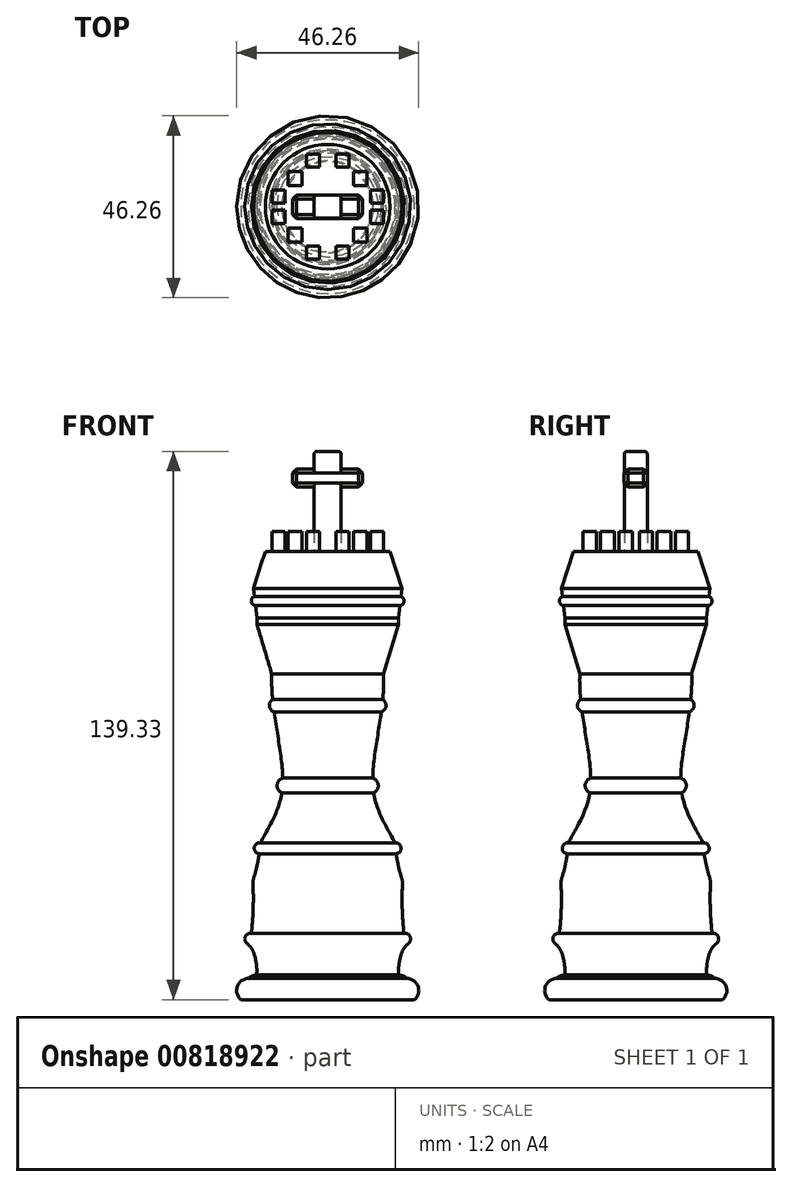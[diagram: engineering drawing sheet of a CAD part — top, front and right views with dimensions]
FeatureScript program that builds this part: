
annotation { "Feature Type Name" : "Feature", "Feature Type Description" : "" }
export const myFeature = defineFeature(function(context is Context, id is Id, definition is map)
    precondition{}
    {
        {
            var Q0;
            Q0=qCreatedBy(makeId("Front.planeOp"),FACE);
            var sketch = newSketch(context, id + "F0", { "sketchPlane" : qUnion([Q0])});
            skLineSegment(sketch, "E0", {"start": v(0, -37.92) * mm, "end": v(0, 63.8) * mm});
            skArc(sketch, "E1", {"start": v(-11.45, 12.13) * mm, "mid": v(-12.85, 10.36) * mm, "end": v(-11.68, 8.42) * mm});
            skArc(sketch, "E2", {"start": v(-14, 32.07) * mm, "mid": v(-14.81, 30.39) * mm, "end": v(-13.62, 28.94) * mm});
            skArc(sketch, "E3", {"start": v(-19.74, -30.2) * mm, "mid": v(-18.98, -22.08) * mm, "end": v(-19.03, -13.92) * mm});
            skFitSpline(sketch, "E4.trimOffspring", {"points": [v(-25.61, -37.92) * mm, v(-19.46, -8.96) * mm, v(-11.68, 8.42) * mm, v(-14.2, 35.39) * mm, v(-12.94, 57.3) * mm, v(-15.84, 63.8) * mm], "startDerivative": vector(16.77, 129.7) * mm, "endDerivative": vector(-31.89, 45.75) * mm});
            skArc(sketch, "E5", {"start": v(-19.03, -13.92) * mm, "mid": v(-17.75, -9.2) * mm, "end": v(-17.15, -4.34) * mm});
            skArc(sketch, "E6", {"start": v(-18.05, -37.92) * mm, "mid": v(-18.31, -33.93) * mm, "end": v(-19.74, -30.2) * mm});
            skArc(sketch, "E7", {"start": v(-17.15, -4.34) * mm, "mid": v(-18.67, -5.58) * mm, "end": v(-17.4, -7.09) * mm});
            skArc(sketch, "E8", {"start": v(-19.38, -27.31) * mm, "mid": v(-21.06, -28.56) * mm, "end": v(-19.74, -30.2) * mm});
            skArc(sketch, "E9", {"start": v(-18.05, -37.92) * mm, "mid": v(-21.18, -41.05) * mm, "end": v(-18.05, -44.17) * mm});
            skArc(sketch, "E10", {"start": v(-20.2, -38.78) * mm, "mid": v(-22.96, -40.84) * mm, "end": v(-22.07, -44.17) * mm});
            skLineSegment(sketch, "E11", {"start": v(-18.05, -44.17) * mm, "end": v(0, -44.17) * mm});
            skLineSegment(sketch, "E12", {"start": v(0, -44.17) * mm, "end": v(0, -37.92) * mm});
            skLineSegment(sketch, "E13", {"start": v(-18.05, -44.17) * mm, "end": v(-22.07, -44.17) * mm});
            skLineSegment(sketch, "E14", {"start": v(-14.2, 38.6) * mm, "end": v(-17.98, 51.2) * mm});
            skLineSegment(sketch, "E15", {"start": v(-15.84, 69.76) * mm, "end": v(0, 69.76) * mm});
            skLineSegment(sketch, "E16", {"start": v(0, 69.76) * mm, "end": v(0, 63.8) * mm});
            skFitSpline(sketch, "E17.trimOffspring", {"points": [v(-25.61, -37.92) * mm, v(-19.46, -8.96) * mm, v(-11.68, 8.42) * mm, v(-14.2, 35.39) * mm, v(-12.94, 57.3) * mm, v(-15.84, 63.8) * mm], "startDerivative": vector(16.77, 129.7) * mm, "endDerivative": vector(-31.89, 45.75) * mm});
            skPoint(sketch, "E18.orphan", {"position": v(-21.75, 63.8) * mm});
            skLineSegment(sketch, "E19", {"start": v(-17.94, 52.8) * mm, "end": v(-18.85, 60.36) * mm});
            skLineSegment(sketch, "E20", {"start": v(-18.85, 60.36) * mm, "end": v(-15.84, 69.76) * mm});
            skLineSegment(sketch, "E21", {"start": v(-17.94, 52.8) * mm, "end": v(-17.98, 51.2) * mm});
            skPoint(sketch, "E22.start.orphan", {"position": v(-18.85, 54.11) * mm});
            skArc(sketch, "E23", {"start": v(-18.6, 58.27) * mm, "mid": v(-19.4, 57) * mm, "end": v(-18.32, 55.95) * mm});
            skSolve(sketch);
        }
        {
            var Q0;
            Q0 = qSketchRegion(id + "F0", true);
            var Q1;
            Q1=sQuery(id+"F0.wireOp",EDGE,"E0");
            revolve(context, id + "F1", {"surfaceOperationType" : NewSurfaceOperationType.NEW, "entities" : qUnion([Q0]), "axis" : qUnion([Q1]), "revolveType" : RevolveType.FULL});
        }
        {
            var Q0;
            Q0=makeQuery(id+"F1.opRevolve","SWEPT_EDGE",EDGE,{"disambiguationData":[OSD([sQuery(id+"F0.wireOp",EDGE,"E3"),sQuery(id+"F0.wireOp",EDGE,"E6")])]});
            var Q1;
            Q1=makeQuery(id+"F1.opRevolve","SWEPT_EDGE",EDGE,{"disambiguationData":[OSD([sQuery(id+"F0.wireOp",EDGE,"E3"),sQuery(id+"F0.wireOp",EDGE,"E5")])]});
            fillet(context, id + "F2", {"entities" : qUnion([Q0, Q1]), "radius" : 5.08 * mm, "tangentPropagation" : true, "allowEdgeOverflow" : false});
        }
        {
            var Q0;
            Q0=makeQuery(id+"F1.opRevolve","SWEPT_FACE",FACE,{"disambiguationData":[OSD([sQuery(id+"F0.wireOp",EDGE,"E15")])]});
            var sketch = newSketch(context, id + "F3", { "sketchPlane" : qUnion([Q0])});
            skLineSegment(sketch, "E24", {"start": v(0, 30.88) * mm, "end": v(0, -30.54) * mm});
            skLineSegment(sketch, "E25", {"start": v(-43.93, 0) * mm, "end": v(35.6, 0) * mm});
            skLineSegment(sketch, "E26.bottom", {"start": v(-5.44, 13.36) * mm, "end": v(-2.12, 13.36) * mm});
            skLineSegment(sketch, "E26.top", {"start": v(-5.44, 10.04) * mm, "end": v(-2.12, 10.04) * mm});
            skLineSegment(sketch, "E26.left", {"start": v(-5.44, 13.36) * mm, "end": v(-5.44, 10.04) * mm});
            skLineSegment(sketch, "E26.right", {"start": v(-2.12, 13.36) * mm, "end": v(-2.12, 10.04) * mm});
            skLineSegment(sketch, "E27.MirrorCS", {"start": v(5.44, 10.04) * mm, "end": v(2.12, 10.04) * mm});
            skLineSegment(sketch, "E28.MirrorCS", {"start": v(5.44, 13.36) * mm, "end": v(5.44, 10.04) * mm});
            skLineSegment(sketch, "E29.MirrorCS", {"start": v(5.44, 13.36) * mm, "end": v(2.12, 13.36) * mm});
            skLineSegment(sketch, "E30.MirrorCS", {"start": v(2.12, 13.36) * mm, "end": v(2.12, 10.04) * mm});
            skLineSegment(sketch, "E31.MirrorCS", {"start": v(-5.44, -10.04) * mm, "end": v(-2.12, -10.04) * mm});
            skLineSegment(sketch, "E32.MirrorCS", {"start": v(-5.44, -13.36) * mm, "end": v(-5.44, -10.04) * mm});
            skLineSegment(sketch, "E33.MirrorCS", {"start": v(-2.12, -13.36) * mm, "end": v(-2.12, -10.04) * mm});
            skLineSegment(sketch, "E34.MirrorCS", {"start": v(-5.44, -13.36) * mm, "end": v(-2.12, -13.36) * mm});
            skLineSegment(sketch, "E35.MirrorCS", {"start": v(2.12, -13.36) * mm, "end": v(2.12, -10.04) * mm});
            skLineSegment(sketch, "E36.MirrorCS", {"start": v(5.44, -13.36) * mm, "end": v(2.12, -13.36) * mm});
            skLineSegment(sketch, "E37.MirrorCS", {"start": v(5.44, -10.04) * mm, "end": v(2.12, -10.04) * mm});
            skLineSegment(sketch, "E38.MirrorCS", {"start": v(5.44, -13.36) * mm, "end": v(5.44, -10.04) * mm});
            skLineSegment(sketch, "E39.bottom", {"start": v(-6.52, 8.95) * mm, "end": v(-10.04, 8.95) * mm});
            skLineSegment(sketch, "E39.top", {"start": v(-6.52, 5.36) * mm, "end": v(-10.04, 5.36) * mm});
            skLineSegment(sketch, "E39.left", {"start": v(-6.52, 8.95) * mm, "end": v(-6.52, 5.36) * mm});
            skLineSegment(sketch, "E39.right", {"start": v(-10.04, 8.95) * mm, "end": v(-10.04, 5.36) * mm});
            skLineSegment(sketch, "E40.MirrorCS", {"start": v(-6.52, -5.36) * mm, "end": v(-10.04, -5.36) * mm});
            skLineSegment(sketch, "E41.MirrorCS", {"start": v(-10.04, -8.95) * mm, "end": v(-10.04, -5.36) * mm});
            skLineSegment(sketch, "E42.MirrorCS", {"start": v(-6.52, -8.95) * mm, "end": v(-6.52, -5.36) * mm});
            skLineSegment(sketch, "E43.MirrorCS", {"start": v(-6.52, -8.95) * mm, "end": v(-10.04, -8.95) * mm});
            skLineSegment(sketch, "E44.MirrorCS", {"start": v(6.52, 8.95) * mm, "end": v(6.52, 5.36) * mm});
            skLineSegment(sketch, "E45.MirrorCS", {"start": v(6.52, 8.95) * mm, "end": v(10.04, 8.95) * mm});
            skLineSegment(sketch, "E46.MirrorCS", {"start": v(10.04, 8.95) * mm, "end": v(10.04, 5.36) * mm});
            skLineSegment(sketch, "E47.MirrorCS", {"start": v(6.52, 5.36) * mm, "end": v(10.04, 5.36) * mm});
            skLineSegment(sketch, "E48.MirrorCS", {"start": v(6.52, -5.36) * mm, "end": v(10.04, -5.36) * mm});
            skLineSegment(sketch, "E49.MirrorCS", {"start": v(10.04, -8.95) * mm, "end": v(10.04, -5.36) * mm});
            skLineSegment(sketch, "E50.MirrorCS", {"start": v(6.52, -8.95) * mm, "end": v(10.04, -8.95) * mm});
            skLineSegment(sketch, "E51.MirrorCS", {"start": v(6.52, -8.95) * mm, "end": v(6.52, -5.36) * mm});
            skLineSegment(sketch, "E52.bottom", {"start": v(-10.86, 4.28) * mm, "end": v(-14.18, 4.28) * mm});
            skLineSegment(sketch, "E52.top", {"start": v(-10.86, 0.89) * mm, "end": v(-14.18, 0.89) * mm});
            skLineSegment(sketch, "E52.left", {"start": v(-10.86, 4.28) * mm, "end": v(-10.86, 0.89) * mm});
            skLineSegment(sketch, "E52.right", {"start": v(-14.18, 4.28) * mm, "end": v(-14.18, 0.89) * mm});
            skLineSegment(sketch, "E53.MirrorCS", {"start": v(-10.86, -4.28) * mm, "end": v(-10.86, -0.89) * mm});
            skLineSegment(sketch, "E54.MirrorCS", {"start": v(-10.86, -4.28) * mm, "end": v(-14.18, -4.28) * mm});
            skLineSegment(sketch, "E55.MirrorCS", {"start": v(-14.18, -4.28) * mm, "end": v(-14.18, -0.89) * mm});
            skLineSegment(sketch, "E56.MirrorCS", {"start": v(-10.86, -0.89) * mm, "end": v(-14.18, -0.89) * mm});
            skLineSegment(sketch, "E57.MirrorCS", {"start": v(10.86, 4.28) * mm, "end": v(10.86, 0.89) * mm});
            skLineSegment(sketch, "E58.MirrorCS", {"start": v(10.86, 4.28) * mm, "end": v(14.18, 4.28) * mm});
            skLineSegment(sketch, "E59.MirrorCS", {"start": v(14.18, -4.28) * mm, "end": v(14.18, -0.89) * mm});
            skLineSegment(sketch, "E60.MirrorCS", {"start": v(10.86, -4.28) * mm, "end": v(10.86, -0.89) * mm});
            skLineSegment(sketch, "E61.MirrorCS", {"start": v(14.18, 4.28) * mm, "end": v(14.18, 0.89) * mm});
            skLineSegment(sketch, "E62.MirrorCS", {"start": v(10.86, -0.89) * mm, "end": v(14.18, -0.89) * mm});
            skLineSegment(sketch, "E63.MirrorCS", {"start": v(10.86, -4.28) * mm, "end": v(14.18, -4.28) * mm});
            skLineSegment(sketch, "E64.MirrorCS", {"start": v(10.86, 0.89) * mm, "end": v(14.18, 0.89) * mm});
            skSolve(sketch);
        }
        {
            var Q0;
            Q0 = qSketchRegion(id + "F3", true);
            extrude(context, id + "F4", {"entities" : qUnion([Q0]), "operationType" : NewBodyOperationType.ADD, "depth" : 5.08 * mm, "offsetDistance" : 25.4 * mm});
        }
        {
            var Q0;
            Q0=makeQuery(id+"F1.opRevolve","SWEPT_FACE",FACE,{"disambiguationData":[OSD([sQuery(id+"F0.wireOp",EDGE,"E15")])]});
            var sketch = newSketch(context, id + "F5", { "sketchPlane" : qUnion([Q0])});
            skLineSegment(sketch, "E65.top", {"start": v(0, 2.93) * mm, "end": v(-3.44, 2.93) * mm});
            skLineSegment(sketch, "E65.right", {"start": v(-3.44, 0) * mm, "end": v(-3.44, 2.93) * mm});
            skLineSegment(sketch, "E66.MirrorCS", {"start": v(0, 2.93) * mm, "end": v(3.44, 2.93) * mm});
            skLineSegment(sketch, "E67.MirrorCS", {"start": v(3.44, 0) * mm, "end": v(3.44, 2.93) * mm});
            skLineSegment(sketch, "E68.MirrorCS", {"start": v(-3.44, 0) * mm, "end": v(-3.44, -2.93) * mm});
            skLineSegment(sketch, "E69.MirrorCS", {"start": v(0, -2.93) * mm, "end": v(-3.44, -2.93) * mm});
            skLineSegment(sketch, "E70.MirrorCS", {"start": v(0, -2.93) * mm, "end": v(3.44, -2.93) * mm});
            skLineSegment(sketch, "E71.MirrorCS", {"start": v(3.44, 0) * mm, "end": v(3.44, -2.93) * mm});
            skPoint(sketch, "E65.bottom.start.orphan", {"position": v(0, 0) * mm});
            skSolve(sketch);
        }
        {
            var Q0;
            Q0 = qSketchRegion(id + "F5", true);
            extrude(context, id + "F6", {"entities" : qUnion([Q0]), "operationType" : NewBodyOperationType.ADD, "depth" : 25.4 * mm, "offsetDistance" : 25.4 * mm});
        }
        {
            var Q0;
            Q0=qCreatedBy(makeId("Right.planeOp"),FACE);
            var sketch = newSketch(context, id + "F7", { "sketchPlane" : qUnion([Q0])});
            skLineSegment(sketch, "E72.bottom", {"start": v(-2.96, 86.09) * mm, "end": v(2.97, 86.09) * mm});
            skLineSegment(sketch, "E72.top", {"start": v(-2.96, 90.63) * mm, "end": v(2.97, 90.63) * mm});
            skLineSegment(sketch, "E72.left", {"start": v(-2.96, 86.09) * mm, "end": v(-2.96, 90.63) * mm});
            skLineSegment(sketch, "E72.right", {"start": v(2.97, 86.09) * mm, "end": v(2.97, 90.63) * mm});
            skSolve(sketch);
        }
        {
            var Q0;
            Q0 = qSketchRegion(id + "F7", true);
            extrude(context, id + "F8", {"entities" : qUnion([Q0]), "operationType" : NewBodyOperationType.ADD, "endBound" : BoundingType.SYMMETRIC, "depth" : 17.78 * mm, "offsetDistance" : 25.4 * mm});
        }
        {
            var Q0;
            Q0=makeQuery(id+"F8.opExtrude","SWEPT_FACE",FACE,{"disambiguationData":[OSD([sQuery(id+"F7.wireOp",EDGE,"E72.left")])]});
            var Q1;
            Q1=makeQuery(id+"F8.opExtrude","SWEPT_FACE",FACE,{"disambiguationData":[OSD([sQuery(id+"F7.wireOp",EDGE,"E72.right")])]});
            var Q2;
            Q2=makeQuery(id+"F8.opExtrude","CAP_FACE",FACE,{"disambiguationData":[OSD([sQuery(id+"F7.wireOp",EDGE,"E72.bottom"),sQuery(id+"F7.wireOp",EDGE,"E72.top"),sQuery(id+"F7.wireOp",EDGE,"E72.left"),sQuery(id+"F7.wireOp",EDGE,"E72.right")])],"isStart":false});
            var Q3;
            Q3=makeQuery(id+"F8.opExtrude","CAP_FACE",FACE,{"disambiguationData":[OSD([sQuery(id+"F7.wireOp",EDGE,"E72.bottom"),sQuery(id+"F7.wireOp",EDGE,"E72.top"),sQuery(id+"F7.wireOp",EDGE,"E72.left"),sQuery(id+"F7.wireOp",EDGE,"E72.right")])],"isStart":true});
            chamfer(context, id + "F9", {"entities" : qUnion([Q0, Q1, Q2, Q3]), "width" : 1.02 * mm, "tangentPropagation" : true});
        }
        {
            var Q0;
            {var subQ0=sQuery(id+"F5.wireOp",EDGE,"E65.top");var subQ1=sQuery(id+"F5.wireOp",EDGE,"E65.right");Q0=makeQuery(id+"F8.boolean.opBoolean","SPLIT",EDGE,{"disambiguationData":[TD([makeQuery(id+"F1.opRevolve","SWEPT_FACE",FACE,{"disambiguationData":[OSD([sQuery(id+"F0.wireOp",EDGE,"E15")])]})])],"derivedFrom":makeQuery(id+"F6.opExtrude","SWEPT_EDGE",EDGE,{"disambiguationData":[OSD([subQ0,subQ1])]})});}
            var Q1;
            {var subQ0=sQuery(id+"F5.wireOp",EDGE,"E68.MirrorCS");var subQ1=sQuery(id+"F5.wireOp",EDGE,"E69.MirrorCS");Q1=makeQuery(id+"F8.boolean.opBoolean","SPLIT",EDGE,{"disambiguationData":[TD([makeQuery(id+"F1.opRevolve","SWEPT_FACE",FACE,{"disambiguationData":[OSD([sQuery(id+"F0.wireOp",EDGE,"E15")])]})])],"derivedFrom":makeQuery(id+"F6.opExtrude","SWEPT_EDGE",EDGE,{"disambiguationData":[OSD([subQ0,subQ1])]})});}
            var Q2;
            {var subQ0=sQuery(id+"F5.wireOp",EDGE,"E66.MirrorCS");var subQ1=sQuery(id+"F5.wireOp",EDGE,"E67.MirrorCS");Q2=makeQuery(id+"F8.boolean.opBoolean","SPLIT",EDGE,{"disambiguationData":[TD([makeQuery(id+"F1.opRevolve","SWEPT_FACE",FACE,{"disambiguationData":[OSD([sQuery(id+"F0.wireOp",EDGE,"E15")])]})])],"derivedFrom":makeQuery(id+"F6.opExtrude","SWEPT_EDGE",EDGE,{"disambiguationData":[OSD([subQ0,subQ1])]})});}
            var Q3;
            {var subQ0=sQuery(id+"F5.wireOp",EDGE,"E71.MirrorCS");var subQ1=sQuery(id+"F5.wireOp",EDGE,"E70.MirrorCS");Q3=makeQuery(id+"F8.boolean.opBoolean","SPLIT",EDGE,{"disambiguationData":[TD([makeQuery(id+"F1.opRevolve","SWEPT_FACE",FACE,{"disambiguationData":[OSD([sQuery(id+"F0.wireOp",EDGE,"E15")])]})])],"derivedFrom":makeQuery(id+"F6.opExtrude","SWEPT_EDGE",EDGE,{"disambiguationData":[OSD([subQ1,subQ0])]})});}
            var Q4;
            {var subQ0=sQuery(id+"F5.wireOp",EDGE,"E71.MirrorCS");var subQ1=sQuery(id+"F5.wireOp",EDGE,"E70.MirrorCS");Q4=makeQuery(id+"F8.boolean.opBoolean","SPLIT",EDGE,{"disambiguationData":[TD([makeQuery(id+"F8.opExtrude","SWEPT_FACE",FACE,{"disambiguationData":[OSD([sQuery(id+"F7.wireOp",EDGE,"E72.top")])]})])],"derivedFrom":makeQuery(id+"F6.opExtrude","SWEPT_EDGE",EDGE,{"disambiguationData":[OSD([subQ1,subQ0])]})});}
            var Q5;
            {var subQ1=sQuery(id+"F5.wireOp",EDGE,"E69.MirrorCS");var subQ2=sQuery(id+"F5.wireOp",EDGE,"E68.MirrorCS");Q5=makeQuery(id+"F8.boolean.opBoolean","SPLIT",EDGE,{"disambiguationData":[TD([makeQuery(id+"F8.opExtrude","SWEPT_FACE",FACE,{"disambiguationData":[OSD([sQuery(id+"F7.wireOp",EDGE,"E72.top")])]})])],"derivedFrom":makeQuery(id+"F6.opExtrude","SWEPT_EDGE",EDGE,{"disambiguationData":[OSD([subQ2,subQ1])]})});}
            var Q6;
            {var subQ1=sQuery(id+"F5.wireOp",EDGE,"E67.MirrorCS");var subQ2=sQuery(id+"F5.wireOp",EDGE,"E66.MirrorCS");Q6=makeQuery(id+"F8.boolean.opBoolean","SPLIT",EDGE,{"disambiguationData":[TD([makeQuery(id+"F8.opExtrude","SWEPT_FACE",FACE,{"disambiguationData":[OSD([sQuery(id+"F7.wireOp",EDGE,"E72.top")])]})])],"derivedFrom":makeQuery(id+"F6.opExtrude","SWEPT_EDGE",EDGE,{"disambiguationData":[OSD([subQ2,subQ1])]})});}
            var Q7;
            {var subQ2=sQuery(id+"F5.wireOp",EDGE,"E65.right");var subQ3=sQuery(id+"F5.wireOp",EDGE,"E65.top");Q7=makeQuery(id+"F8.boolean.opBoolean","SPLIT",EDGE,{"disambiguationData":[TD([makeQuery(id+"F8.opExtrude","SWEPT_FACE",FACE,{"disambiguationData":[OSD([sQuery(id+"F7.wireOp",EDGE,"E72.top")])]})])],"derivedFrom":makeQuery(id+"F6.opExtrude","SWEPT_EDGE",EDGE,{"disambiguationData":[OSD([subQ3,subQ2])]})});}
            var Q8;
            Q8=makeQuery(id+"F6.opExtrude","CAP_EDGE",EDGE,{"disambiguationData":[OSD([sQuery(id+"F5.wireOp",EDGE,"E65.top"),sQuery(id+"F5.wireOp",EDGE,"E66.MirrorCS")])],"isStart":false});
            var Q9;
            Q9=makeQuery(id+"F6.opExtrude","CAP_EDGE",EDGE,{"disambiguationData":[OSD([sQuery(id+"F5.wireOp",EDGE,"E67.MirrorCS"),sQuery(id+"F5.wireOp",EDGE,"E71.MirrorCS")])],"isStart":false});
            var Q10;
            Q10=makeQuery(id+"F6.opExtrude","CAP_EDGE",EDGE,{"disambiguationData":[OSD([sQuery(id+"F5.wireOp",EDGE,"E69.MirrorCS"),sQuery(id+"F5.wireOp",EDGE,"E70.MirrorCS")])],"isStart":false});
            var Q11;
            Q11=makeQuery(id+"F6.opExtrude","CAP_EDGE",EDGE,{"disambiguationData":[OSD([sQuery(id+"F5.wireOp",EDGE,"E65.right"),sQuery(id+"F5.wireOp",EDGE,"E68.MirrorCS")])],"isStart":false});
            fillet(context, id + "F10", {"entities" : qUnion([Q0, Q1, Q2, Q3, Q4, Q5, Q6, Q7, Q8, Q9, Q10, Q11]), "radius" : 0.76 * mm, "tangentPropagation" : true, "allowEdgeOverflow" : false});
        }
    });
